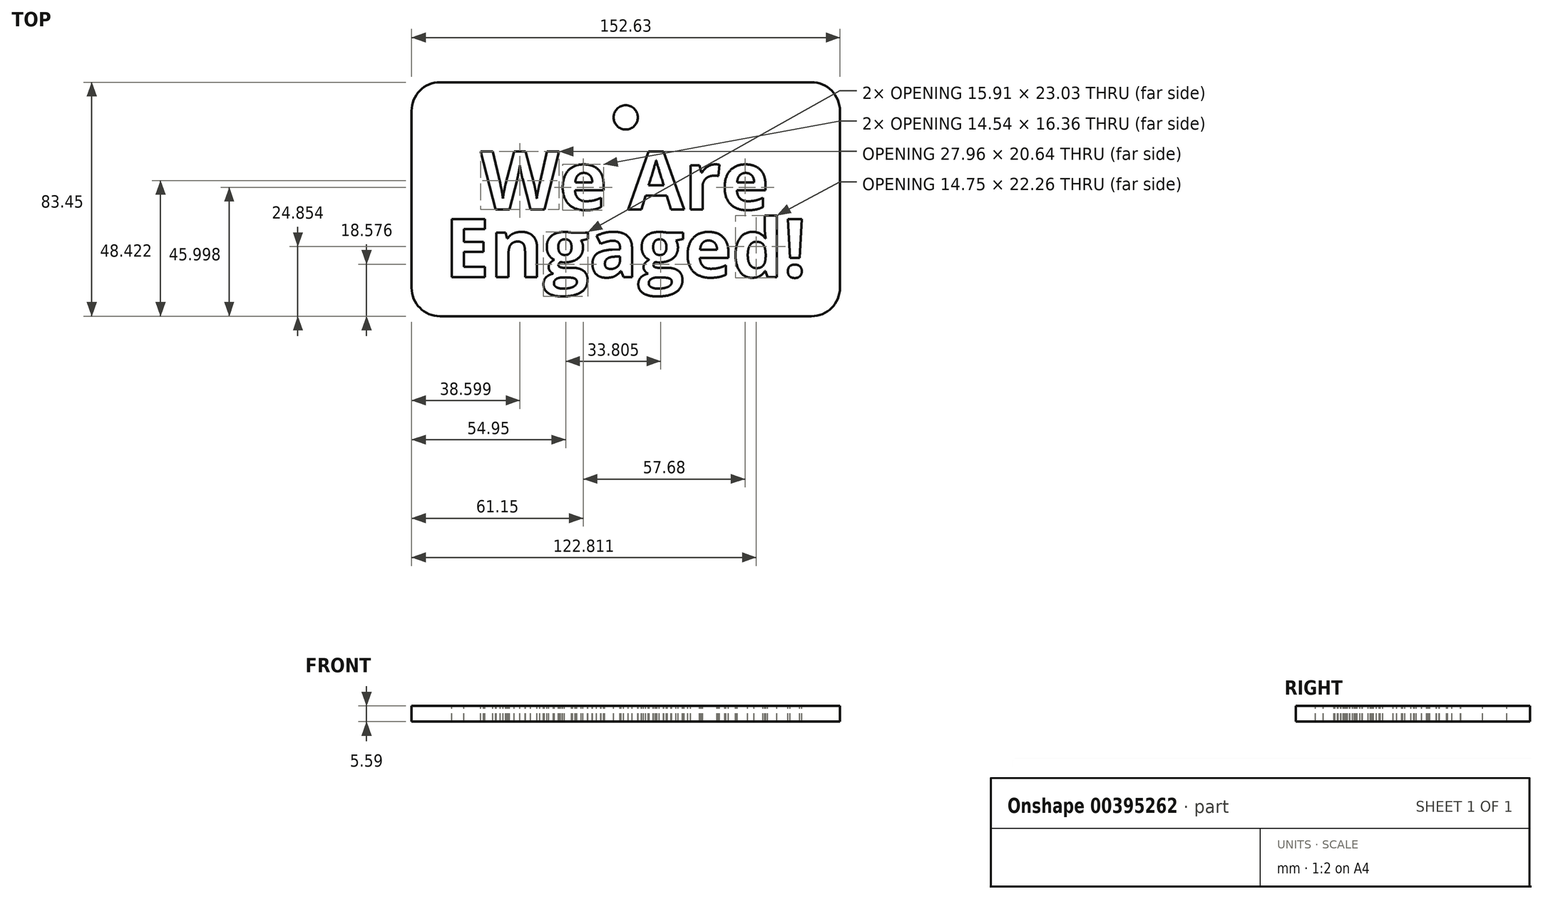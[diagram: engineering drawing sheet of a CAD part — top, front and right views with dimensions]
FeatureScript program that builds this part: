
annotation { "Feature Type Name" : "Feature", "Feature Type Description" : "" }
export const myFeature = defineFeature(function(context is Context, id is Id, definition is map)
    precondition{}
    {
        {
            var Q0;
            Q0=qCreatedBy(makeId("Top.planeOp"),FACE);
            var sketch = newSketch(context, id + "F0", { "sketchPlane" : qUnion([Q0])});
            skText(sketch, "E0", { "text": "We Are", "fontName": "OpenSans-Bold.ttf"});
            skText(sketch, "E1", { "text": "Engaged!", "fontName": "OpenSans-Bold.ttf"});
            skCircle(sketch, "E2", {"center": v(0, 26.58) * mm, "radius": 4.33 * mm});
            const initialGuessF0  = {"E0": [-0.05169, -0.00625, 1, 0, 0.02082], "E1": [-0.0646, -0.03034, 1, 0, 0.02082]};
            skSetInitialGuess(sketch, initialGuessF0);
            skSolve(sketch);
        }
        {
            var Q0;
            Q0=qCreatedBy(makeId("Top.planeOp"),FACE);
            var sketch = newSketch(context, id + "F1", { "sketchPlane" : qUnion([Q0])});
            skLineSegment(sketch, "E3.bottom", {"start": v(-76.3, 39.1) * mm, "end": v(76.32, 39.1) * mm});
            skLineSegment(sketch, "E3.top", {"start": v(-76.3, -44.35) * mm, "end": v(76.32, -44.35) * mm});
            skLineSegment(sketch, "E3.left", {"start": v(-76.3, 39.1) * mm, "end": v(-76.3, -44.35) * mm});
            skLineSegment(sketch, "E3.right", {"start": v(76.32, 39.1) * mm, "end": v(76.32, -44.35) * mm});
            skSolve(sketch);
        }
        {
            var Q0;
            Q0 = qSketchRegion(id + "F1", true);
            extrude(context, id + "F2", {"entities" : qUnion([Q0]), "depth" : 5.6 * mm});
        }
        {
            var Q0;
            Q0 = qSketchRegion(id + "F0", true);
            extrude(context, id + "F3", {"entities" : qUnion([Q0]), "operationType" : NewBodyOperationType.REMOVE, "oppositeDirection" : true, "depth" : 38.86 * mm, "hasSecondDirection" : true, "secondDirectionOppositeDirection" : false, "secondDirectionDepth" : 25.4 * mm});
        }
        {
            var Q0;
            Q0=makeQuery(id+"F2.opExtrude","SWEPT_EDGE",EDGE,{"disambiguationData":[OSD([sQuery(id+"F1.wireOp",EDGE,"E3.top"),sQuery(id+"F1.wireOp",EDGE,"E3.left")])]});
            fillet(context, id + "F4", {"entities" : qUnion([Q0]), "radius" : 10.16 * mm, "tangentPropagation" : true, "allowEdgeOverflow" : false});
        }
        {
            var Q0;
            Q0=makeQuery(id+"F2.opExtrude","SWEPT_EDGE",EDGE,{"disambiguationData":[OSD([sQuery(id+"F1.wireOp",EDGE,"E3.bottom"),sQuery(id+"F1.wireOp",EDGE,"E3.left")])]});
            fillet(context, id + "F5", {"entities" : qUnion([Q0]), "radius" : 10.16 * mm, "tangentPropagation" : true, "allowEdgeOverflow" : false});
        }
        {
            var Q0;
            Q0=makeQuery(id+"F2.opExtrude","SWEPT_EDGE",EDGE,{"disambiguationData":[OSD([sQuery(id+"F1.wireOp",EDGE,"E3.bottom"),sQuery(id+"F1.wireOp",EDGE,"E3.right")])]});
            var Q1;
            Q1=makeQuery(id+"F2.opExtrude","SWEPT_EDGE",EDGE,{"disambiguationData":[OSD([sQuery(id+"F1.wireOp",EDGE,"E3.top"),sQuery(id+"F1.wireOp",EDGE,"E3.right")])]});
            fillet(context, id + "F6", {"entities" : qUnion([Q0, Q1]), "radius" : 10.16 * mm, "tangentPropagation" : true, "allowEdgeOverflow" : false});
        }
    });
